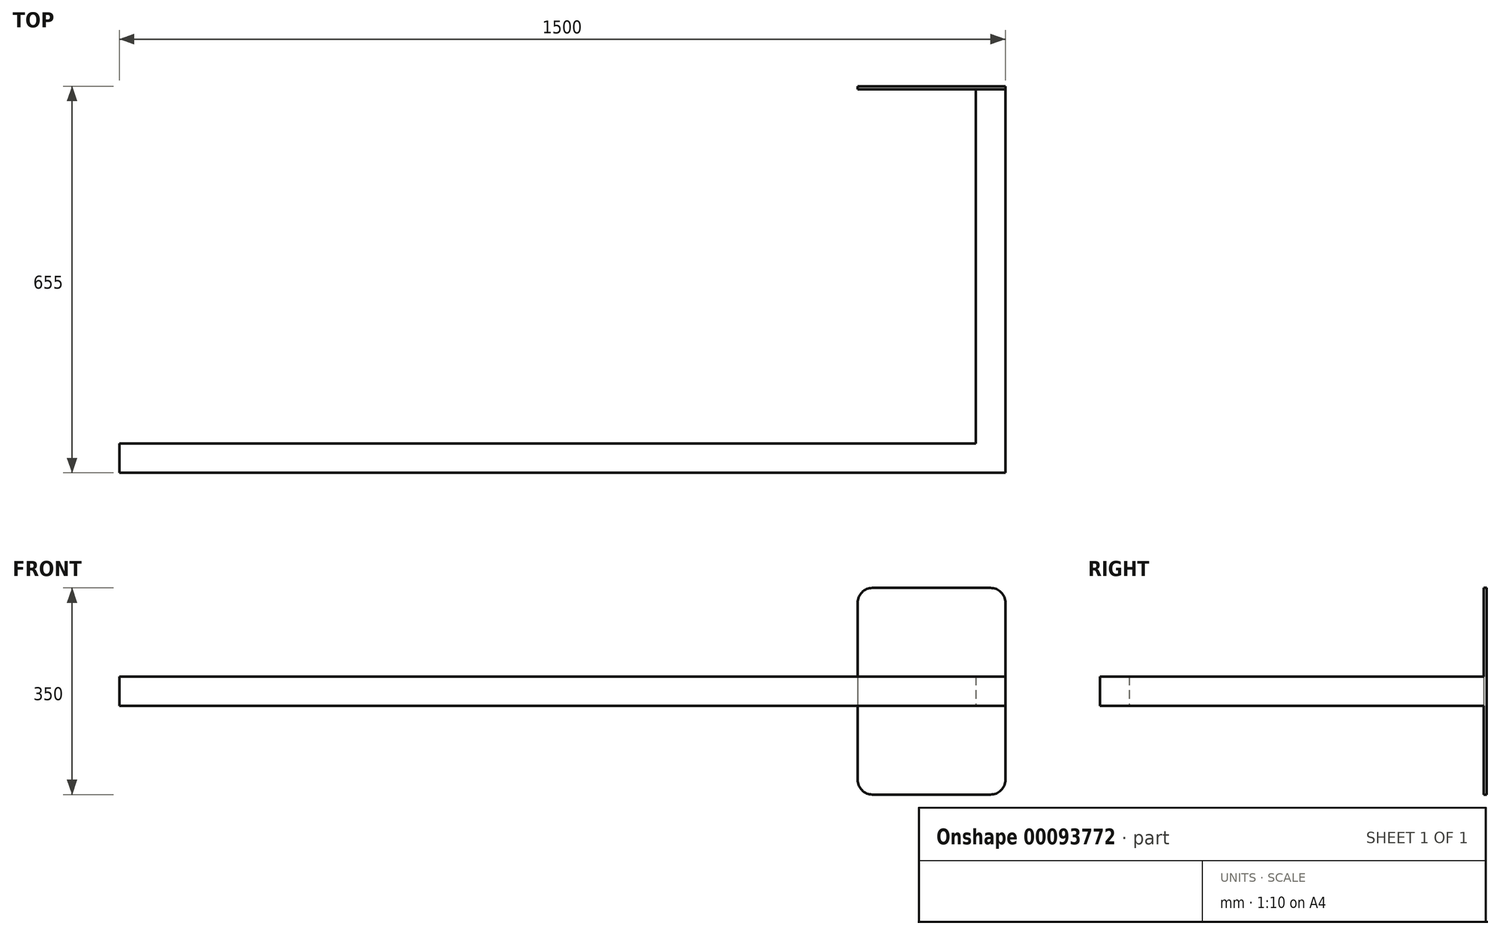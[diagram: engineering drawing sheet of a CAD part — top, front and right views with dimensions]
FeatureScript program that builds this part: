
annotation { "Feature Type Name" : "Feature", "Feature Type Description" : "" }
export const myFeature = defineFeature(function(context is Context, id is Id, definition is map)
    precondition{}
    {
        {
            var Q0;
            Q0=qCreatedBy(makeId("Front.planeOp"),FACE);
            var sketch = newSketch(context, id + "F0", { "sketchPlane" : qUnion([Q0])});
            skLineSegment(sketch, "E0.bottom", {"start": v(0, 0) * mm, "end": v(1500, 0) * mm});
            skLineSegment(sketch, "E0.top", {"start": v(0, -50) * mm, "end": v(1500, -50) * mm});
            skLineSegment(sketch, "E0.left", {"start": v(0, 0) * mm, "end": v(0, -50) * mm});
            skLineSegment(sketch, "E0.right", {"start": v(1500, 0) * mm, "end": v(1500, -50) * mm});
            skSolve(sketch);
        }
        {
            var Q0;
            Q0=makeQuery(id+"F0.imprint","IMPRINT",FACE,{"disambiguationData":[TD([[makeQuery(id+"F0.imprint","IMPRINT",EDGE,{"derivedFrom":sQuery(id+"F0.wireOp",EDGE,"E0.bottom")}),-1.0]])]});
            extrude(context, id + "F1", {"entities" : qUnion([Q0]), "depth" : 50 * mm});
        }
        {
            var Q0;
            Q0=makeQuery(id+"F1.opExtrude","CAP_FACE",FACE,{"disambiguationData":[OSD([sQuery(id+"F0.wireOp",EDGE,"E0.bottom"),sQuery(id+"F0.wireOp",EDGE,"E0.top"),sQuery(id+"F0.wireOp",EDGE,"E0.left"),sQuery(id+"F0.wireOp",EDGE,"E0.right")])],"isStart":true});
            var sketch = newSketch(context, id + "F2", { "sketchPlane" : qUnion([Q0])});
            skLineSegment(sketch, "E1.bottom", {"start": v(-1500, 0) * mm, "end": v(-1450, 0) * mm});
            skLineSegment(sketch, "E1.top", {"start": v(-1500, -50) * mm, "end": v(-1450, -50) * mm});
            skLineSegment(sketch, "E1.left", {"start": v(-1500, 0) * mm, "end": v(-1500, -50) * mm});
            skLineSegment(sketch, "E1.right", {"start": v(-1450, 0) * mm, "end": v(-1450, -50) * mm});
            skSolve(sketch);
        }
        {
            var Q0;
            Q0=makeQuery(id+"F2.imprint","IMPRINT",FACE,{"disambiguationData":[TD([[makeQuery(id+"F2.imprint","IMPRINT",EDGE,{"derivedFrom":sQuery(id+"F2.wireOp",EDGE,"E1.bottom")}),1.0]])]});
            extrude(context, id + "F3", {"entities" : qUnion([Q0]), "operationType" : NewBodyOperationType.ADD, "depth" : 600 * mm});
        }
        {
            var Q0;
            Q0=makeQuery(id+"F3.opExtrude","CAP_FACE",FACE,{"disambiguationData":[OSD([sQuery(id+"F2.wireOp",EDGE,"E1.bottom"),sQuery(id+"F2.wireOp",EDGE,"E1.top"),sQuery(id+"F2.wireOp",EDGE,"E1.left"),sQuery(id+"F2.wireOp",EDGE,"E1.right")])],"isStart":false});
            var sketch = newSketch(context, id + "F4", { "sketchPlane" : qUnion([Q0])});
            skLineSegment(sketch, "E2.bottom", {"start": v(-1475, 150) * mm, "end": v(-1275, 150) * mm});
            skLineSegment(sketch, "E2.top", {"start": v(-1475, -200) * mm, "end": v(-1275, -200) * mm});
            skLineSegment(sketch, "E2.left", {"start": v(-1500, 125) * mm, "end": v(-1500, -175) * mm});
            skLineSegment(sketch, "E2.right", {"start": v(-1250, 125) * mm, "end": v(-1250, -175) * mm});
            skPoint(sketch, "E3.visualSharp", {"position": v(-1500, 150) * mm});
            skArc(sketch, "E3.filletArc", {"start": v(-1475, 150) * mm, "mid": v(-1492.68, 142.68) * mm, "end": v(-1500, 125) * mm});
            skPoint(sketch, "E4.visualSharp", {"position": v(-1250, 150) * mm});
            skArc(sketch, "E4.filletArc", {"start": v(-1250, 125) * mm, "mid": v(-1257.32, 142.68) * mm, "end": v(-1275, 150) * mm});
            skPoint(sketch, "E5.visualSharp", {"position": v(-1250, -200) * mm});
            skArc(sketch, "E5.filletArc", {"start": v(-1275, -200) * mm, "mid": v(-1257.32, -192.68) * mm, "end": v(-1250, -175) * mm});
            skPoint(sketch, "E6.visualSharp", {"position": v(-1500, -200) * mm});
            skArc(sketch, "E6.filletArc", {"start": v(-1500, -175) * mm, "mid": v(-1492.68, -192.68) * mm, "end": v(-1475, -200) * mm});
            skSolve(sketch);
        }
        {
            var Q0;
            {var subQ4=sQuery(id+"F4.wireOp",EDGE,"E2.bottom");Q0=makeQuery(id+"F4.imprint","IMPRINT",FACE,{"disambiguationData":[TD([[makeQuery(id+"F4.imprint","IMPRINT",EDGE,{"derivedFrom":subQ4}),-1.0]])]});}
            var Q1;
            {var subQ1=makeQuery(id+"F3.opExtrude","CAP_EDGE",EDGE,{"disambiguationData":[OSD([sQuery(id+"F2.wireOp",EDGE,"E1.bottom")])],"isStart":false});Q1=makeQuery(id+"F4.imprint","IMPRINT",FACE,{"disambiguationData":[TD([[makeQuery(id+"F4.imprint","IMPRINT",EDGE,{"derivedFrom":subQ1}),1.0]])]});}
            extrude(context, id + "F5", {"entities" : qUnion([Q0, Q1]), "operationType" : NewBodyOperationType.ADD, "depth" : 5 * mm});
        }
    });
